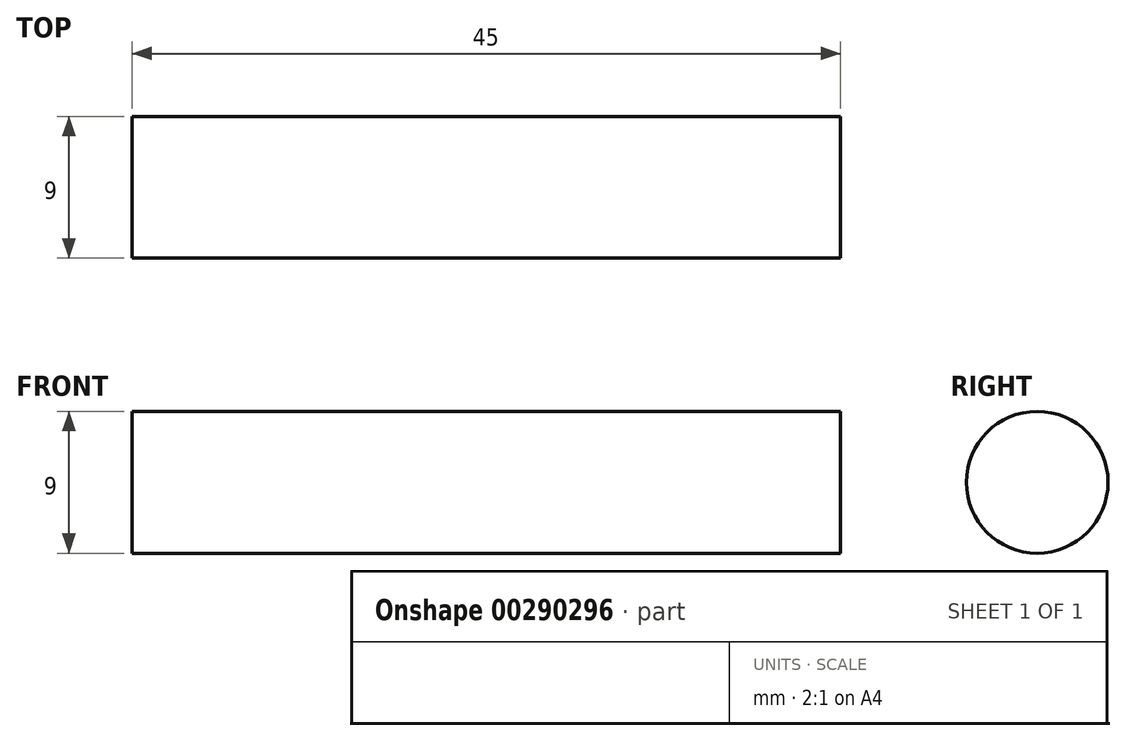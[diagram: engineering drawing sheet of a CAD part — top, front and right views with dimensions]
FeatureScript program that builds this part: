
annotation { "Feature Type Name" : "Feature", "Feature Type Description" : "" }
export const myFeature = defineFeature(function(context is Context, id is Id, definition is map)
    precondition{}
    {
        {
            var Q0;
            Q0=qCreatedBy(makeId("Front.planeOp"),FACE);
            var sketch = newSketch(context, id + "F0", { "sketchPlane" : qUnion([Q0])});
            skLineSegment(sketch, "E0", {"start": v(0, 4.5) * mm, "end": v(22.5, 4.5) * mm});
            skLineSegment(sketch, "E1", {"start": v(22.5, 4.5) * mm, "end": v(22.5, 0) * mm});
            skLineSegment(sketch, "E2", {"start": v(22.5, 0) * mm, "end": v(0, 0) * mm});
            skLineSegment(sketch, "E3.MirrorCS", {"start": v(-22.5, 0) * mm, "end": v(0, 0) * mm});
            skLineSegment(sketch, "E4.MirrorCS", {"start": v(0, 4.5) * mm, "end": v(-22.5, 4.5) * mm});
            skLineSegment(sketch, "E5.MirrorCS", {"start": v(-22.5, 4.5) * mm, "end": v(-22.5, 0) * mm});
            skSolve(sketch);
        }
        {
            var Q0;
            Q0 = qSketchRegion(id + "F0", true);
            var Q1;
            Q1=sQuery(id+"F0.wireOp",EDGE,"E3.MirrorCS");
            revolve(context, id + "F1", {"entities" : qUnion([Q0]), "axis" : qUnion([Q1]), "revolveType" : RevolveType.FULL});
        }
    });
